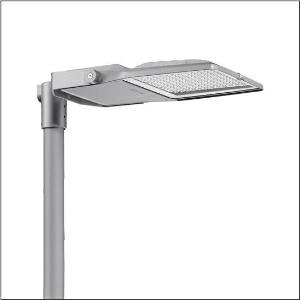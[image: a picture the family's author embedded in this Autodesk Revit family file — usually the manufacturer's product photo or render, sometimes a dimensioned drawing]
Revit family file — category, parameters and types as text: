
# Revit family: floodlight_fl_21_iq_midi___pl61_5xa7782e2c3a_85c4
name_source: partatom
category: Lighting Fixtures
units: mm (PartAtom-declared; Revit-internal decimal feet)

## family parameters
Cut with Voids When Loaded = No
Host = Face
Light Source = No
Part Type = Normal
Room Calculation Point = No
Round Connector Dimension = Use Diameter
Shared = No

## types (1)
- --- (1 x LED, 26360 lm, 208.1 W, 3000K)
    Apparent Load = 208 VA
    CIE Flux Codes = 33 65 98 100 100
    Color Rendering = 70
    Color Temperature = 3000K
    Default Elevation = 1800 mm
    Description = Floodlight FL 21 iQ midi, floodlight, primary light control with lens, of PMMA, primary optical cover: protective disc, of toughened safety glass, transparent, light distribution: PL61, light emission: direct distribution, installation type: surface-mounted, LED, High Power LED, rated luminous flux: 26.360lm, luminous efficacy: 127lm/W, light colour: 730, colour temperature: 3000K, control gear: ECG iQ, control: optimised constant luminous flux control (CLO 2.0), Desk-Remote (wireless, voltage-free reading and setting of iQ features in the workshop via application-optimized NFC function/RFID function), Smart-Wire, Night-Set, Temp-Guard, Auto-Match, Street-Remote, with terminal, 6-pole, mains connection: 220..240V, AC, 50/60Hz, start of lifetime: 208W, end of service life: 227W, reduction: 90W, luminaire housing, of diecast aluminium, powder-coated, Siteco® metallic grey (DB 702S), corrosivity category C5 mid according to DIN EN ISO 12944, sealing non-destructively replaceable, please order mast flange separately, mast bracket, of steel, galvanised, powder-coated, Siteco® metallic grey (DB 702S), protection rating (complete): IP66, insulation class (complete): insulation class II (safety insulation), certification: CE, protection symbol: D, impact resistance: IK08, permissible operating ambient temperature: -40..+40°C, permissible operating ambient temperature for outdoor applications: -40..+50°C, standard: DIN EN 12944, LABS conformity tested according to VDMA 24364:2018-05, packaging unit: 1 piece

Light Distribution: PL61
    Height = 76 mm
    Lamp = 1 x LED
    Lamp Light Flux = 26360 lm
    Lamp Power = 208.1 W
    Lamp count = 1
    Length = 657 mm
    Luminous efficacy = 127 lm/W
    Manufacturer = Siteco
    ModVariant = No
    Model = 5XA7782E2C3A
    Number of Poles = 1
    OnlyDefault = Yes
    Power Factor = 1
    Product Name = Floodlight FL 21 iQ midi | PL61
    Product group = floodlight | pylon annexe
    ProductGroupID = 6200
    Protection Class = Protection class II
    Protection Degree = IP 66
    RLX_Detail_Level = 1
    RLX_Emergency_Light_Flux = 0 lm
    RLX_Emergency_Type = 0
    RLX_Emergency_Type_DB = No
    RlxData = <blob elided: 153777 chars, md5=210f814c>
    Socket = socket
    Standby Power = 0 W
    System Light Flux = 26360 lm
    System Power = 208 W
    Type Comments = factory setting: luminous flux: 100 % | dim-lin: 254 | 710 mA
    Type Image = l_1007123.jpg
    URL = http://relux.com
    VarID = @adj_057033
    Voltage = 0 V
    Weight = 0.00 kg
    Width = 442 mm

## geometry (parser evidence)
native form markers: Blend x4, Sweep x12
no freeform markers — native parametric forms only
